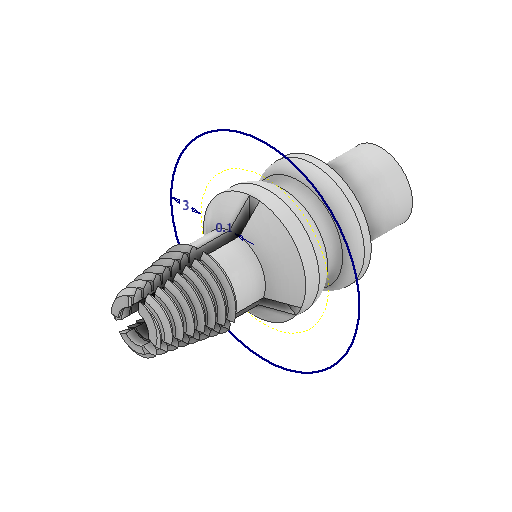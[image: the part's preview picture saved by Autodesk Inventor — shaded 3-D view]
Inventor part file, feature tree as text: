
AUTODESK INVENTOR PART (.ipt)
format: ipt  version: 2022 (Build 260153000, 153)  size: 1,212,928 bytes
history: native  units: in
note: dims shown in document units (in); Inventor stores cm internally (conversion verified against a paired STEP export)
features: sketch x15, extrude x8, other x6, revolve x4, reference x4, projected_geometry x2, plane x1, sweep x1, chamfer x1, fillet x1
ambient origin geometry x8: Origin, YZ Plane, XZ Plane, XY Plane, X Axis, Y Axis, Z Axis, Center Point
bodies: Solid1 (feature_tree)
feature tree (43):
  other  "00_selfcenter_2mm_thread_v1.ipt"
  revolve  "Revolution1"  [1 undecoded]
  extrude  "Extrusion2"  TaperAngle=0.0deg  [1 undecoded]
  sketch  "Sketch4"  dims[d11=0.3937in d12=360.0deg]
  plane  "Work Plane1"
  revolve  "Revolution2"  Angle=360.0deg
  sweep  "Sweep1"
  revolve  "Revolution3"  [1 undecoded]
  extrude  "Extrusion4"  TaperAngle=0.0deg  [1 undecoded]
  extrude  "Extrusion5"  Depth=0.3937in
  extrude  "Extrusion6"  TaperAngle=0.0deg  [1 undecoded]
  chamfer  "Chamfer1"  Distance=0.3937in
  extrude  "Extrusion8"  Depth=0.2362in
  extrude  "Extrusion9"  Depth=0.2362in
  extrude  "Extrusion10"  Depth=0.2362in
  revolve  "Revolution4"  [1 undecoded]
  fillet  "Fillet2"  Radius=0.0394in
  extrude  "Extrusion11"  Depth=0.2362in TaperAngle=45.0deg
  sketch  "Sketch2"  dims[d4=0.2165in d5=0.0984in]
  sketch  "Sketch3"  dims[d7=0.0394in d10=0.0in]
  projected_geometry  "Projected Loop1"
  reference  "Reference3"
  reference  "Reference4"
  sketch  "Sketch5"  dims[d14=0.0787in d15=0.0591in]
  sketch  "3D Sketch1"
  other  "Helical Curve1"
  sketch  "Sketch7"  dims[d16=0.0in d17=0.0in d18=0.0039in]
  sketch  "Sketch8"  dims[d19=0.1181in d22=0.0in]
  sketch  "Sketch9"  dims[d23=0.3937in d24=0.0394in]
  reference  "Reference6"
  projected_geometry  "Projected Loop2"
  sketch  "Sketch10"  dims[d25=360.0deg]
  sketch  "Sketch11"  dims[d26=0.0in d27=0.0in d28=0.0394in d29=0.0977in d30=0.29in d31=3.1496in d32=0.1872in d39=0.0in d40=0.0in]
  sketch  "Sketch13"  dims[d41=0.0394in]
  sketch  "Sketch14"  dims[d42=90.0deg]
  sketch  "Sketch15"  dims[d43=0.0591in]
  reference  "Reference7"
  sketch  "Sketch16"  dims[d44=0.0394in d45=0.3937in d46=0.0in]
  sketch  "Sketch17"  dims[d47=1.1811in d49=360.0deg d51=0.2362in d52=0.29in d53=0.1969in d54=0.1575in d55=0.0in d56=0.0394in d57=0.0in d58=0.0787in d59=0.0787in d60=45.0deg d67=0.0in d68=0.0in d69=0.0in d70=0.0in d71=0.2362in d72=0.0in d73=0.0787in d74=90.0deg d75=0.0787in d76=0.1181in d77=0.0in d78=0.0in]
  other  "Assembly_Cube_Lightsheet_FEPTube_Rotational_v3.iam"
  other  "00_Bearing_US:1"
  other  "<userpath>\Documents\GitHub\Guinardia\INVENTOR\Assembly_Guinardia_V1.iam"
  other  "Assembly_Guinardia_V1.iam"
note: 6 required parameter values undecoded (feature->parameter linkage not recoverable at this tier; creation-order binding heuristic only, values carry confidence <= 0.55)